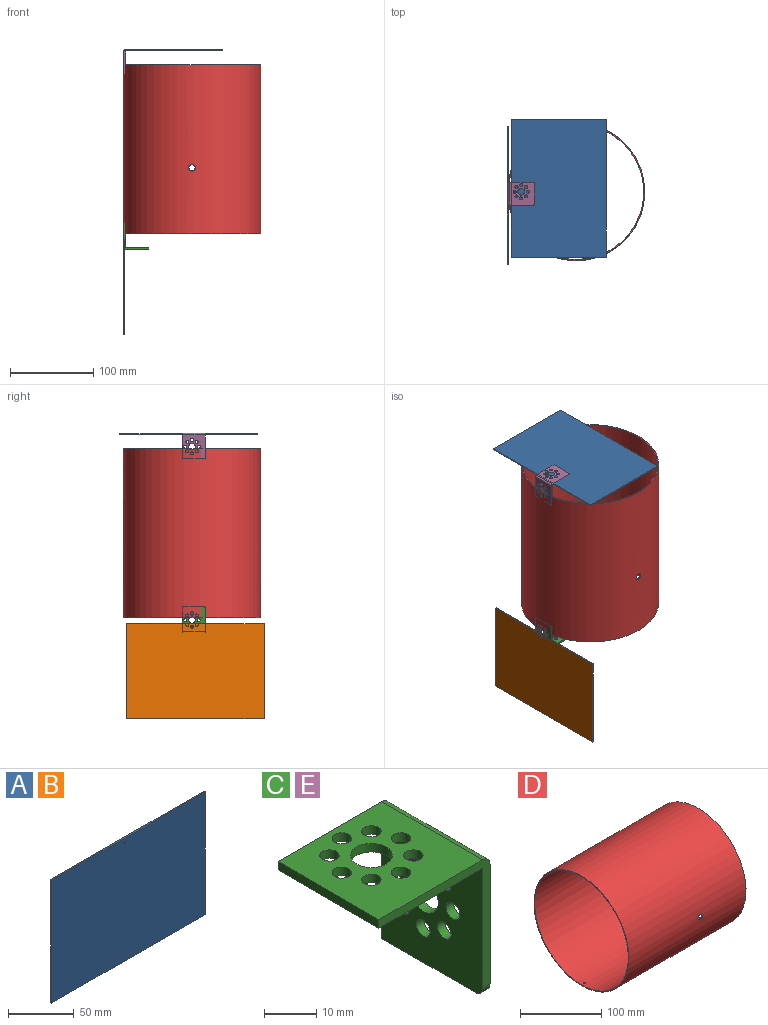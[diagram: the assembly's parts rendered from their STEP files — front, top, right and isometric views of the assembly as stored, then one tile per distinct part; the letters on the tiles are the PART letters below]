
ASSEMBLY  parts=5 mates=4
PART A: 7 faces, bbox 165.1x1.3x114.3 mm
  f0: plane 114.3x1.25mm, normal (-1,0,0), area 142.9mm2, adj f1,f3,f4,f5
  f1: plane 165.1x1.25mm, normal (0,0,-1), area 206.4mm2, adj f0,f2,f4,f5
  f2: plane 114.3x1.25mm, normal (1,0,0), area 142.9mm2, adj f1,f3,f4,f5
  f3: plane 165.1x1.25mm, normal (0,0,1), area 206.4mm2, adj f0,f2,f4,f5
  f4: plane 165.1x114.3mm, normal (0,-1,0), area 18868.3mm2, adj f0,f1,f2,f3,f6
  f5: plane 165.1x114.3mm, normal (0,1,0), area 18868.3mm2, adj f0,f1,f2,f3,f6
  f6: cylinder r=0.92mm len=1.84mm, axis (0,1,0), area 7.2mm2, adj f4,f5
PART B: same geometry as A
PART C: 30 faces, bbox 30x27.2x32 mm
  f0: plane 30x27.21mm, normal (1,0,0), area 679mm2, adj f2,f5,f6,f7,f8,f9,f10,f11
  f1: plane 27.99x27.22mm, normal (0,0,1), area 625.7mm2, adj f5,f6,f16,f17,f18,f19,f20,f21
  f2: plane 25.21x2mm, normal (0,0,-1), area 50.4mm2, adj f0,f3,f25,f27
  f3: plane 30x27.21mm, normal (-1,0,0), area 679mm2, adj f2,f4,f6,f7,f8,f9,f10,f11
  f4: plane 27.99x27.22mm, normal (0,0,-1), area 625.7mm2, adj f3,f6,f16,f17,f18,f19,f20,f21
  f5: cylinder r=2mm len=27.21mm, axis (0,-1,0), area 85.5mm2, adj f0,f1,f6,f27
  f6: plane 30x29.99mm, normal (0,-1,0), area 115.1mm2, adj f0,f1,f3,f4,f5,f25,f26
  f7: cylinder r=1.85mm len=3.7mm, axis (1,0,0), area 23.2mm2, adj f0,f3
  f8: cylinder r=1.85mm len=3.7mm, axis (1,0,0), area 23.2mm2, adj f0,f3
  f9: cylinder r=1.85mm len=3.7mm, axis (1,0,0), area 23.2mm2, adj f0,f3
  f10: cylinder r=1.85mm len=3.7mm, axis (1,0,0), area 23.2mm2, adj f0,f3
  f11: cylinder r=1.85mm len=3.7mm, axis (1,0,0), area 23.2mm2, adj f0,f3
  f12: cylinder r=1.85mm len=3.7mm, axis (1,0,0), area 23.2mm2, adj f0,f3
  f13: cylinder r=4mm len=8mm, axis (1,0,0), area 50.3mm2, adj f0,f3
  f14: cylinder r=1.85mm len=3.7mm, axis (1,0,0), area 23.2mm2, adj f0,f3
  f15: cylinder r=1.85mm len=3.7mm, axis (1,0,0), area 23.2mm2, adj f0,f3
  f16: cylinder r=1.85mm len=3.7mm, axis (0,0,1), area 23.2mm2, adj f1,f4
  f17: cylinder r=1.85mm len=3.7mm, axis (0,0,1), area 23.2mm2, adj f1,f4
  f18: cylinder r=1.85mm len=3.7mm, axis (0,0,1), area 23.2mm2, adj f1,f4
  f19: cylinder r=1.85mm len=3.7mm, axis (0,0,1), area 23.2mm2, adj f1,f4
  f20: cylinder r=1.85mm len=3.7mm, axis (0,0,1), area 23.2mm2, adj f1,f4
  f21: cylinder r=1.85mm len=3.7mm, axis (0,0,1), area 23.2mm2, adj f1,f4
  f22: cylinder r=1.85mm len=3.7mm, axis (0,0,1), area 23.2mm2, adj f1,f4
  f23: cylinder r=1.85mm len=3.7mm, axis (0,0,1), area 23.2mm2, adj f1,f4
  f24: cylinder r=4mm len=8mm, axis (0,0,1), area 50.3mm2, adj f1,f4
  f25: cylinder r=2mm len=2mm, axis (1,0,0), area 6.3mm2, adj f0,f2,f3,f6
  f26: plane 27.22x2mm, normal (-1,0,0), area 54.4mm2, adj f1,f4,f6,f29
  f27: plane 32x2.08mm, normal (0,1,0), area 63.3mm2, adj f0,f1,f2,f3,f4,f5,f28
  f28: plane 2x0.01mm, normal (1,0,0), area 0mm2, adj f1,f4,f27,f29
  f29: plane 27.91x2mm, normal (0,1,0), area 55.8mm2, adj f1,f4,f26,f28
PART D: 8 faces, bbox 203.2x165.1x165.1 mm
  f0: cylinder r=81.28mm len=203.2mm, axis (-1,0,0), area 103657.6mm2, adj f2,f3,f4,f5,f6,f7
  f1: cylinder r=82.55mm len=203.2mm, axis (-1,0,0), area 105279.1mm2, adj f2,f3,f4,f5,f6,f7
  f2: plane 165.1x165.1mm, normal (1,0,0), area 653.7mm2, adj f0,f1
  f3: plane 165.1x165.1mm, normal (-1,0,0), area 653.7mm2, adj f0,f1
  f4: cylinder r=4.01mm len=8.02mm, axis (0,-1,0), area 32mm2, adj f0,f1
  f5: cylinder r=4.01mm len=8.02mm, axis (0,1,0), area 32mm2, adj f0,f1
  f6: cylinder r=1.5mm len=3mm, axis (0,0,1), area 12mm2, adj f0,f1
  f7: cylinder r=1.5mm len=3mm, axis (0,0,1), area 12mm2, adj f0,f1
PART E: same geometry as C
PLACE A rot(axis=(-0.58,-0.58,0.58),120deg) t=(36.47,-73.83,118.67)mm
PLACE B rot(axis=(0,0,-1),90deg) t=(-81.28,73.83,-222.67)mm
PLACE C rot(axis=(0,1,0),180deg) t=(-65.91,-16,-104.29)mm
PLACE D rot(axis=(0,1,0),90deg) t=(0,0,101.6)mm
PLACE E rot(axis=(0,-1,0),90deg) t=(-65.91,-16,104.29)mm
MATE fastened B.f6 <-> C.f12  axis (1,0,0) through (-81.91,0,-112.29)mm
MATE fastened E.f20 <-> D.f7  axis (-1,0,0) through (-81.91,0,96.29)mm
MATE fastened E.f12 <-> A.f6  axis (0,0,1) through (-73.91,0,119.29)mm
MATE fastened C.f14 <-> D.f6  axis (-1,0,0) through (-81.91,0,-96.29)mm
